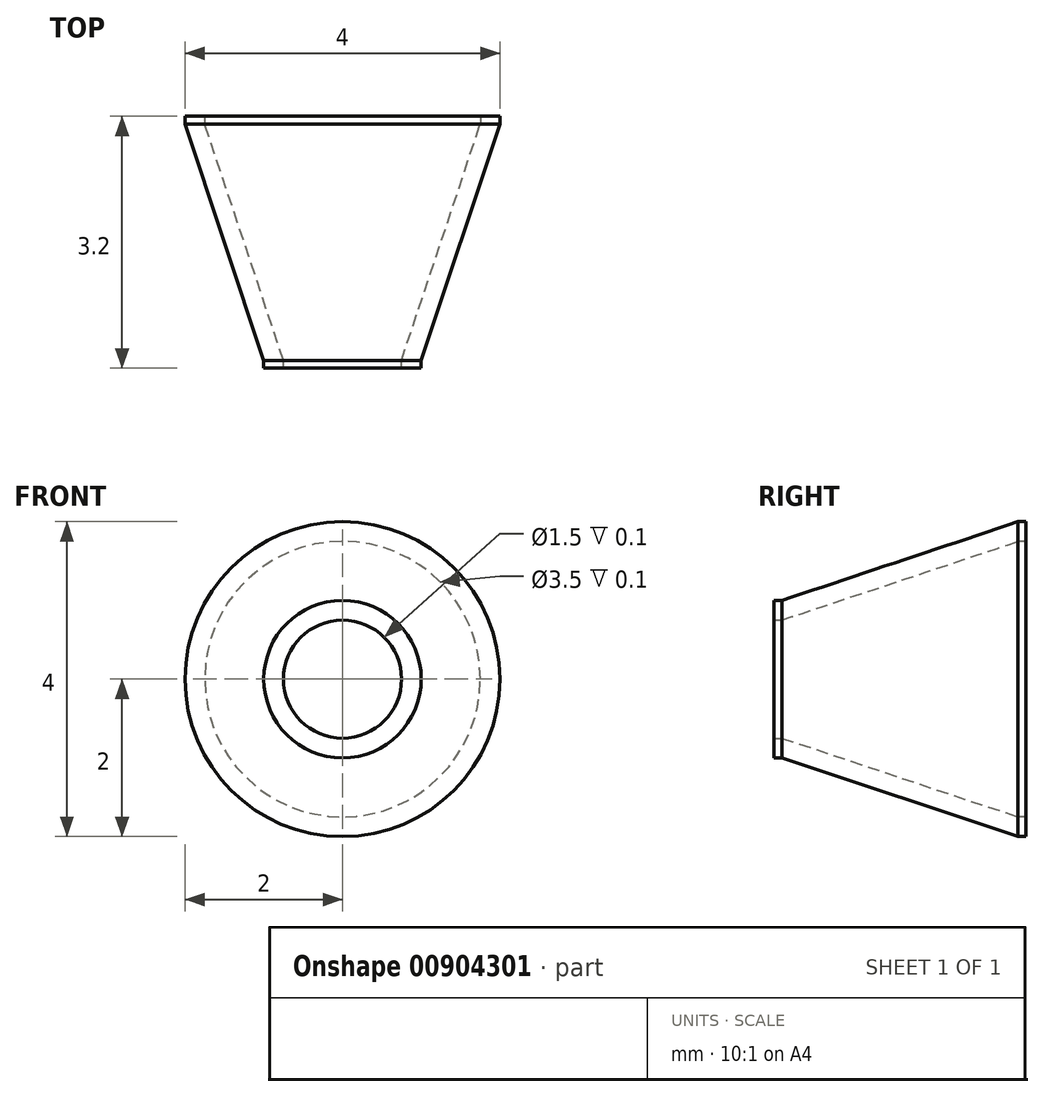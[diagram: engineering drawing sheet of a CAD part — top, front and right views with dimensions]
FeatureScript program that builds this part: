
annotation { "Feature Type Name" : "Feature", "Feature Type Description" : "" }
export const myFeature = defineFeature(function(context is Context, id is Id, definition is map)
    precondition{}
    {
        {
            var Q0;
            Q0=qCreatedBy(makeId("Front.planeOp"),FACE);
            cPlane(context, id + "F0", {"entities" : qUnion([Q0]), "cplaneType" : CPlaneType.OFFSET, "offset" : 3 * mm, "width" : 150 * mm, "height" : 150 * mm});
        }
        {
            var Q0;
            Q0=qCreatedBy(makeId("Front.planeOp"),FACE);
            var sketch = newSketch(context, id + "F1", { "sketchPlane" : qUnion([Q0])});
            skCircle(sketch, "E0", {"center": v(0, 0) * mm, "radius": 2 * mm});
            skCircle(sketch, "E1", {"center": v(0, 0) * mm, "radius": 1.75 * mm});
            skSolve(sketch);
        }
        {
            var Q0;
            Q0=qCreatedBy(id+"F0.planeOp",FACE);
            var sketch = newSketch(context, id + "F2", { "sketchPlane" : qUnion([Q0])});
            skCircle(sketch, "E2", {"center": v(0, 0) * mm, "radius": 0.75 * mm});
            skCircle(sketch, "E3", {"center": v(0, 0) * mm, "radius": 1 * mm});
            skSolve(sketch);
        }
        {
            var Q0;
            Q0=makeQuery(id+"F2.imprint","IMPRINT",FACE,{"disambiguationData":[TD([[makeQuery(id+"F2.imprint","IMPRINT",EDGE,{"derivedFrom":sQuery(id+"F2.wireOp",EDGE,"E2")}),-1.0]])]});
            extrude(context, id + "F3", {"entities" : qUnion([Q0]), "depth" : 2 * mm, "offsetDistance" : 25 * mm});
        }
        {
            var Q0;
            Q0=makeQuery(id+"F1.imprint","IMPRINT",FACE,{"disambiguationData":[TD([[makeQuery(id+"F1.imprint","IMPRINT",EDGE,{"derivedFrom":sQuery(id+"F1.wireOp",EDGE,"E0")}),1.0]])]});
            extrude(context, id + "F4", {"entities" : qUnion([Q0]), "oppositeDirection" : true, "depth" : 2 * mm, "offsetDistance" : 25 * mm});
        }
        {
            var Q0;
            Q0=qCreatedBy(makeId("Right.planeOp"),FACE);
            var sketch = newSketch(context, id + "F5", { "sketchPlane" : qUnion([Q0])});
            skLineSegment(sketch, "E4.0", {"start": v(0, -2) * mm, "end": v(0, 2) * mm});
            skLineSegment(sketch, "E5.0", {"start": v(-3, -1) * mm, "end": v(-3, 1) * mm});
            skLineSegment(sketch, "E6.0", {"start": v(-3, -0.75) * mm, "end": v(-3, 0.75) * mm});
            skLineSegment(sketch, "E7.0", {"start": v(0, -1.75) * mm, "end": v(0, 1.75) * mm});
            skLineSegment(sketch, "E8", {"start": v(0, -1.75) * mm, "end": v(-3, -0.75) * mm});
            skLineSegment(sketch, "E9", {"start": v(0, -2) * mm, "end": v(-3, -1) * mm});
            skLineSegment(sketch, "E10", {"start": v(0, 0) * mm, "end": v(-3, 0) * mm});
            skSolve(sketch);
        }
        {
            var Q0;
            {var subQ2=sQuery(id+"F5.wireOp",EDGE,"E8");Q0=makeQuery(id+"F5.imprint","IMPRINT",FACE,{"disambiguationData":[TD([[makeQuery(id+"F5.imprint","IMPRINT",EDGE,{"derivedFrom":subQ2}),1.0]])]});}
            var Q1;
            Q1=sQuery(id+"F5.wireOp",EDGE,"E10");
            revolve(context, id + "F6", {"surfaceOperationType" : NewSurfaceOperationType.NEW, "entities" : qUnion([Q0]), "axis" : qUnion([Q1]), "revolveType" : RevolveType.FULL});
        }
        {
            var Q0;
            Q0=makeQuery(id+"F3.opExtrude","CAP_FACE",FACE,{"disambiguationData":[OSD([sQuery(id+"F2.wireOp",EDGE,"E2"),sQuery(id+"F2.wireOp",EDGE,"E3")])],"isStart":false});
            extrude(context, id + "F7", {"entities" : qUnion([Q0]), "operationType" : NewBodyOperationType.REMOVE, "oppositeDirection" : true, "depth" : 1.9 * mm, "offsetDistance" : 25 * mm});
        }
        {
            var Q0;
            Q0=makeQuery(id+"F4.opExtrude","CAP_FACE",FACE,{"disambiguationData":[OSD([sQuery(id+"F1.wireOp",EDGE,"E0"),sQuery(id+"F1.wireOp",EDGE,"E1")])],"isStart":false});
            extrude(context, id + "F8", {"entities" : qUnion([Q0]), "operationType" : NewBodyOperationType.REMOVE, "oppositeDirection" : true, "depth" : 1.9 * mm, "offsetDistance" : 25 * mm});
        }
    });
